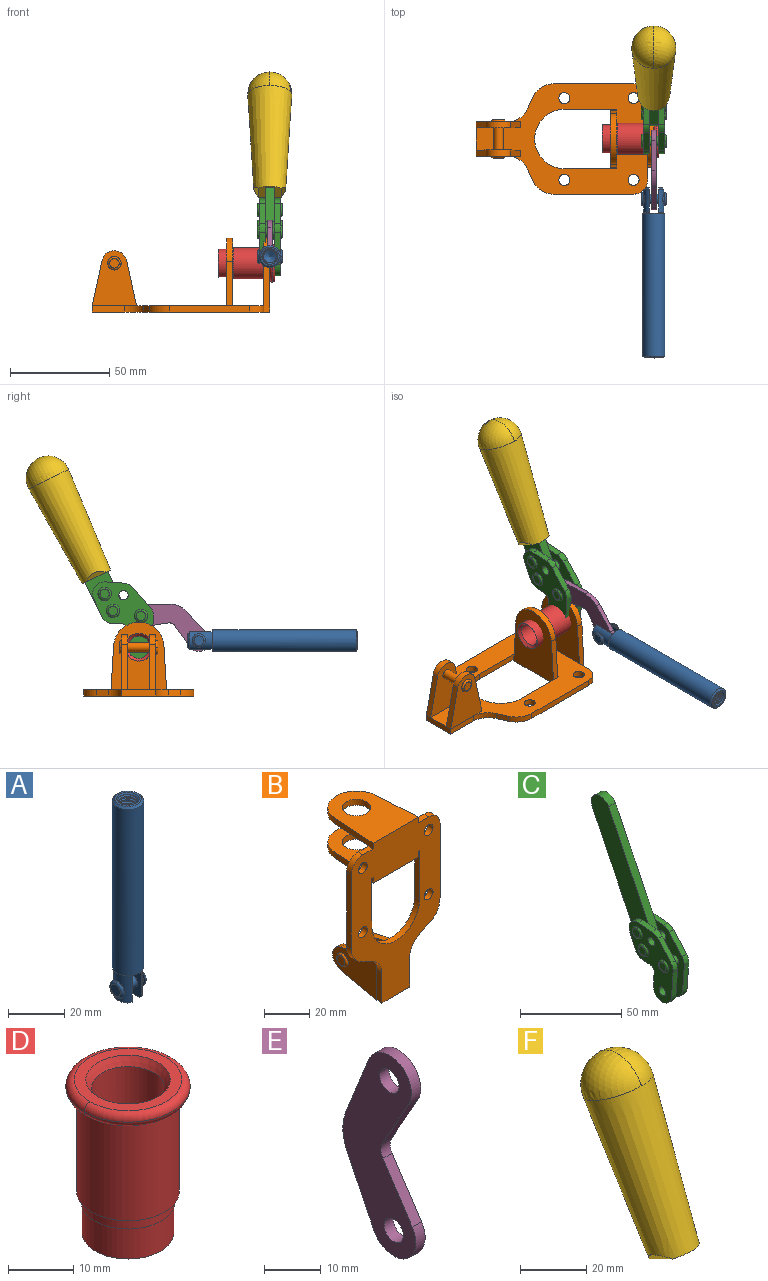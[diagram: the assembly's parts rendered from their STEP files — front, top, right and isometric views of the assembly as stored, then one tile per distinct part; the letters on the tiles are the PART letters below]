
ASSEMBLY  parts=6 mates=6
PART A: 48 faces, bbox 12.6x11.1x86.1 mm
  f0: torus R=2.41mm, axis (-1,0,0), area 15mm2, adj f30,f32,f34
  f1: torus R=2.41mm, axis (-1,0,0), area 15mm2, adj f29,f31,f33
  f2: cylinder r=5.54mm len=72.39mm, axis (0,0,1), area 2518.5mm2, adj f3,f4,f42,f43
  f3: cone r=5.54mm half-angle=45deg, axis (0,0,1), area 7.6mm2, adj f2,f5,f41
  f4: cone r=5.54mm half-angle=45deg, axis (0,0,-1), area 34.9mm2, adj f2,f39
  f5: cylinder r=5.08mm len=11.48mm, axis (0,0,1), area 108.3mm2, adj f3,f7,f8,f41
  f6: cylinder r=2.41mm len=4.83mm, axis (-1,0,0), area 71.2mm2, adj f40,f41
  f7: cylinder r=2.41mm len=4.83mm, axis (-1,0,0), area 7.6mm2, adj f5,f34
  f8: cone r=5.08mm half-angle=45deg, axis (0,0,1), area 10.6mm2, adj f5,f37,f41
  f9: cone r=3.98mm half-angle=45deg, axis (0,0,1), area 17.6mm2, adj f27,f39,f45,f46,f47
  f10: cylinder r=2.41mm len=4.83mm, axis (-1,0,0), area 7.6mm2, adj f33,f38
  f11: cylinder r=3.2mm len=6.4mm, axis (0,0,1), area 78.4mm2, adj f12,f28,f44,f45,f47
  f12: cylinder r=3.2mm len=6.4mm, axis (0,0,1), area 10.5mm2, adj f11,f13,f45,f47
  f13: cylinder r=3.2mm len=6.4mm, axis (0,0,1), area 10.5mm2, adj f12,f14,f45,f47
  f14: cylinder r=3.2mm len=6.4mm, axis (0,0,1), area 10.5mm2, adj f13,f15,f45,f47
  f15: cylinder r=3.2mm len=6.4mm, axis (0,0,1), area 10.5mm2, adj f14,f16,f45,f47
  f16: cylinder r=3.2mm len=6.4mm, axis (0,0,1), area 10.5mm2, adj f15,f17,f45,f47
  f17: cylinder r=3.2mm len=6.4mm, axis (0,0,1), area 10.5mm2, adj f16,f18,f45,f47
  f18: cylinder r=3.2mm len=6.4mm, axis (0,0,1), area 10.5mm2, adj f17,f19,f45,f47
  f19: cylinder r=3.2mm len=6.4mm, axis (0,0,1), area 10.5mm2, adj f18,f20,f45,f47
  f20: cylinder r=3.2mm len=6.4mm, axis (0,0,1), area 10.5mm2, adj f19,f21,f45,f47
  f21: cylinder r=3.2mm len=6.4mm, axis (0,0,1), area 10.5mm2, adj f20,f22,f45,f47
  f22: cylinder r=3.2mm len=6.4mm, axis (0,0,1), area 10.5mm2, adj f21,f23,f45,f47
  f23: cylinder r=3.2mm len=6.4mm, axis (0,0,1), area 10.5mm2, adj f22,f24,f45,f47
  f24: cylinder r=3.2mm len=6.4mm, axis (0,0,1), area 10.5mm2, adj f23,f25,f45,f47
  f25: cylinder r=3.2mm len=6.4mm, axis (0,0,1), area 10.5mm2, adj f24,f26,f45,f47
  f26: cylinder r=3.2mm len=6.4mm, axis (0,0,1), area 10.5mm2, adj f25,f27,f45,f47
  f27: cylinder r=3.2mm len=6.4mm, axis (0,0,1), area 7.4mm2, adj f9,f26,f45,f47
  f28: cone r=3.2mm half-angle=60deg, axis (0,0,1), area 37.2mm2, adj f11
  f29: plane 4.83x4.83mm, normal (-1,0,0), area 18.3mm2, adj f1,f31
  f30: plane 4.83x4.83mm, normal (1,0,0), area 18.3mm2, adj f0,f32
  f31: torus R=2.41mm, axis (-1,0,0), area 15mm2, adj f1,f29,f33
  f32: torus R=2.41mm, axis (-1,0,0), area 15mm2, adj f0,f30,f34
  f33: plane 6.83x6.83mm, normal (1,0,0), area 18.3mm2, adj f1,f10,f31
  f34: plane 6.83x6.83mm, normal (-1,0,0), area 18.3mm2, adj f0,f7,f32
  f35: cone r=5.08mm half-angle=45deg, axis (0,0,1), area 10.6mm2, adj f36,f38,f40
  f36: plane 7.25x1.97mm, normal (0,0,-1), area 10mm2, adj f35,f40
  f37: plane 7.25x1.97mm, normal (0,0,-1), area 10mm2, adj f8,f41
  f38: cylinder r=5.08mm len=11.48mm, axis (0,0,1), area 108.3mm2, adj f10,f35,f40,f42
  f39: plane 9.55x9.55mm, normal (0,0,1), area 22mm2, adj f4,f9
  f40: plane 12.76x10.09mm, normal (1,0,0), area 95.7mm2, adj f6,f35,f36,f38,f42,f43
  f41: plane 12.76x10.09mm, normal (-1,0,0), area 95.7mm2, adj f3,f5,f6,f8,f37,f43
  f42: cone r=5.54mm half-angle=45deg, axis (0,0,1), area 7.6mm2, adj f2,f38,f40
  f43: plane 11.07x4.7mm, normal (0,0,-1), area 50.4mm2, adj f2,f40,f41
  f44: plane 0.89x0.62mm, normal (-1,0,0), area 0.3mm2, adj f11,f45,f46,f47
  f45: bspline ~24.8x7.63mm, area 266.6mm2, adj f9,f11,f12,f13,f14,f15,f16,f17
  f46: bspline ~24.87x7.63mm, area 73.6mm2, adj f9,f44,f45,f47
  f47: bspline ~24.98x7.63mm, area 272.5mm2, adj f9,f11,f12,f13,f14,f15,f16,f17
PART B: 55 faces, bbox 55.7x37.4x89.8 mm
  f0: torus R=2.41mm, axis (-1,0,0), area 15mm2, adj f11,f15,f25
  f1: torus R=2.41mm, axis (-1,0,0), area 15mm2, adj f10,f12,f22
  f2: cylinder r=2.78mm len=5.56mm, axis (0,-1,0), area 54.2mm2, adj f30,f54
  f3: cylinder r=14.99mm len=29.97mm, axis (0,-1,0), area 145.9mm2, adj f30,f49,f53,f54
  f4: cylinder r=2.78mm len=5.56mm, axis (0,-1,0), area 54.2mm2, adj f30,f54
  f5: cylinder r=2.78mm len=5.56mm, axis (0,-1,0), area 54.2mm2, adj f30,f54
  f6: cylinder r=2.78mm len=5.56mm, axis (0,-1,0), area 54.2mm2, adj f30,f54
  f7: cylinder r=6.35mm len=12.7mm, axis (0,0,1), area 123.6mm2, adj f27,f51
  f8: cylinder r=6.35mm len=12.7mm, axis (0,0,-1), area 124.7mm2, adj f21,f35
  f9: cylinder r=2.41mm len=11.18mm, axis (-1,0,0), area 169.4mm2, adj f16,f19
  f10: plane 4.83x4.83mm, normal (1,0,0), area 18.3mm2, adj f1,f12
  f11: plane 4.83x4.83mm, normal (-1,0,0), area 18.3mm2, adj f0,f15
  f12: torus R=2.41mm, axis (-1,0,0), area 15mm2, adj f1,f10,f22
  f13: cylinder r=6.35mm len=12.41mm, axis (1,0,0), area 53.4mm2, adj f18,f19,f22,f23
  f14: cylinder r=6.35mm len=12.41mm, axis (-1,0,0), area 53.4mm2, adj f16,f17,f24,f25
  f15: torus R=2.41mm, axis (-1,0,0), area 15mm2, adj f0,f11,f25
  f16: plane 27.86x22.35mm, normal (1,0,0), area 425.4mm2, adj f9,f14,f17,f24,f30
  f17: plane 22.86x4.97mm, normal (0,0.21,0.98), area 72.5mm2, adj f14,f16,f25,f30
  f18: plane 22.86x4.97mm, normal (0,0.21,0.98), area 72.5mm2, adj f13,f19,f22,f30
  f19: plane 27.86x22.35mm, normal (-1,0,0), area 425.4mm2, adj f9,f13,f18,f23,f30
  f20: cylinder r=12.7mm len=25.35mm, axis (0,0,-1), area 119.8mm2, adj f21,f34,f35,f36
  f21: plane 34.21x28.07mm, normal (0,0,-1), area 702.4mm2, adj f8,f20,f30,f34,f36
  f22: plane 27.96x22.45mm, normal (1,0,0), area 407.2mm2, adj f1,f12,f13,f18,f23,f30,f42,f43
  f23: plane 22.86x4.97mm, normal (0,0.21,-0.98), area 72.5mm2, adj f13,f19,f22,f44
  f24: plane 22.86x4.97mm, normal (0,0.21,-0.98), area 72.5mm2, adj f14,f16,f25,f44
  f25: plane 27.86x22.35mm, normal (-1,0,0), area 407.1mm2, adj f0,f14,f15,f17,f24,f30,f45,f46
  f26: plane 3.1x0.95mm, normal (0,0,-1), area 2.7mm2, adj f30,f49,f50,f54
  f27: plane 34.21x28.07mm, normal (0,0,1), area 702.4mm2, adj f7,f28,f30,f50,f52
  f28: cylinder r=12.7mm len=25.35mm, axis (0,0,1), area 118.8mm2, adj f27,f50,f51,f52
  f29: plane 3.1x0.95mm, normal (0,0,-1), area 2.7mm2, adj f30,f52,f53,f54
  f30: plane 86.54x55.63mm, normal (0,1,0), area 2362.9mm2, adj f2,f3,f4,f5,f6,f16,f17,f18
  f31: plane 40.56x3.1mm, normal (-1,0,0), area 125.7mm2, adj f30,f32,f48,f54
  f32: cylinder r=7.11mm len=7.11mm, axis (0,-1,0), area 34.6mm2, adj f30,f31,f33,f54
  f33: plane 6.67x3.1mm, normal (0,0,1), area 20.4mm2, adj f30,f32,f34,f54
  f34: plane 25.39x3.13mm, normal (-1,0.06,0), area 79.5mm2, adj f20,f21,f33,f35,f54
  f35: plane 37.31x28.45mm, normal (0,0,1), area 789.9mm2, adj f8,f20,f34,f36,f54
  f36: plane 25.39x3.13mm, normal (1,0.06,0), area 79.5mm2, adj f20,f21,f35,f37,f54
  f37: plane 6.67x3.1mm, normal (0,0,1), area 20.4mm2, adj f30,f36,f38,f54
  f38: cylinder r=7.11mm len=7.11mm, axis (0,-1,0), area 34.6mm2, adj f30,f37,f39,f54
  f39: plane 40.56x3.1mm, normal (1,0,0), area 125.7mm2, adj f30,f38,f40,f54
  f40: cylinder r=11.18mm len=10.16mm, axis (0,-1,0), area 39.5mm2, adj f30,f39,f41,f54
  f41: plane 6.09x3.1mm, normal (0.42,0,-0.91), area 20.8mm2, adj f30,f40,f42,f54
  f42: cylinder r=11.18mm len=9.41mm, axis (0,-1,0), area 37.2mm2, adj f22,f30,f41,f43,f54
  f43: plane 16.5x3.1mm, normal (1,0,0), area 51.1mm2, adj f22,f42,f44,f54
  f44: plane 17.37x3.1mm, normal (0,0,-1), area 53.8mm2, adj f23,f24,f30,f43,f45,f54
  f45: plane 16.5x3.1mm, normal (-1,0,0), area 51.1mm2, adj f25,f44,f46,f54
  f46: cylinder r=11.18mm len=9.41mm, axis (0,-1,0), area 37.2mm2, adj f25,f30,f45,f47,f54
  f47: plane 6.09x3.1mm, normal (-0.42,0,-0.91), area 20.8mm2, adj f30,f46,f48,f54
  f48: cylinder r=11.18mm len=10.16mm, axis (0,-1,0), area 39.5mm2, adj f30,f31,f47,f54
  f49: plane 26.54x3.1mm, normal (-1,0,0), area 82.3mm2, adj f3,f26,f30,f54
  f50: plane 25.39x3.1mm, normal (1,0.06,0), area 78.8mm2, adj f26,f27,f28,f51,f54
  f51: plane 37.31x28.45mm, normal (0,0,-1), area 789.9mm2, adj f7,f28,f50,f52,f54
  f52: plane 25.39x3.1mm, normal (-1,0.06,0), area 78.8mm2, adj f27,f28,f29,f51,f54
  f53: plane 26.54x3.1mm, normal (1,0,0), area 82.3mm2, adj f3,f29,f30,f54
  f54: plane 89.66x55.63mm, normal (0,-1,0), area 2678.5mm2, adj f2,f3,f4,f5,f6,f26,f29,f31
PART C: 59 faces, bbox 12.9x60.2x99.6 mm
  f0: torus R=2.39mm, axis (-1,0,0), area 14.9mm2, adj f20,f43,f51
  f1: torus R=2.39mm, axis (-1,0,0), area 14.9mm2, adj f19,f42,f51
  f2: torus R=2.39mm, axis (-1,0,0), area 14.9mm2, adj f18,f35,f51
  f3: torus R=2.39mm, axis (-1,0,0), area 14.9mm2, adj f14,f17,f23
  f4: torus R=2.39mm, axis (-1,0,0), area 14.9mm2, adj f13,f16,f23
  f5: torus R=2.39mm, axis (-1,0,0), area 14.9mm2, adj f12,f15,f23
  f6: cylinder r=2.39mm len=4.78mm, axis (1,0,0), area 46.5mm2, adj f48,f50,f51
  f7: cylinder r=2.39mm len=4.78mm, axis (1,0,0), area 46.5mm2, adj f50,f51
  f8: cylinder r=6.35mm len=12.68mm, axis (1,0,0), area 61.8mm2, adj f38,f39,f50,f51
  f9: cylinder r=2.39mm len=4.78mm, axis (-1,0,0), area 70.5mm2, adj f46,f50
  f10: cylinder r=2.39mm len=4.78mm, axis (-1,0,0), area 46.5mm2, adj f23,f45,f46
  f11: cylinder r=2.39mm len=4.78mm, axis (-1,0,0), area 46.5mm2, adj f23,f46
  f12: plane 4.78x4.78mm, normal (1,0,0), area 17.9mm2, adj f5,f15
  f13: plane 4.78x4.78mm, normal (1,0,0), area 17.9mm2, adj f4,f16
  f14: plane 4.78x4.78mm, normal (1,0,0), area 17.9mm2, adj f3,f17
  f15: torus R=2.39mm, axis (-1,0,0), area 14.9mm2, adj f5,f12,f23
  f16: torus R=2.39mm, axis (-1,0,0), area 14.9mm2, adj f4,f13,f23
  f17: torus R=2.39mm, axis (-1,0,0), area 14.9mm2, adj f3,f14,f23
  f18: plane 4.78x4.78mm, normal (-1,0,0), area 17.9mm2, adj f2,f35
  f19: plane 4.78x4.78mm, normal (-1,0,0), area 17.9mm2, adj f1,f42
  f20: plane 4.78x4.78mm, normal (-1,0,0), area 17.9mm2, adj f0,f43
  f21: plane 2.26x0.2mm, normal (1,0,0), area 0.2mm2, adj f31,f44
  f22: plane 2.26x0.2mm, normal (-1,0,0), area 0.2mm2, adj f41,f44
  f23: plane 39.37x30.77mm, normal (1,0,0), area 565.5mm2, adj f3,f4,f5,f10,f11,f15,f16,f17
  f24: cylinder r=6.1mm len=4.15mm, axis (-1,0,0), area 14.7mm2, adj f23,f25,f32,f46
  f25: plane 10.25x9.01mm, normal (0,-0.75,0.66), area 42.3mm2, adj f23,f24,f26,f46
  f26: cylinder r=6.35mm len=4.64mm, axis (-1,0,0), area 15.6mm2, adj f23,f25,f27,f46
  f27: plane 15.84x3.1mm, normal (0,-1,-0.07), area 49.2mm2, adj f23,f26,f28,f46
  f28: cylinder r=6.35mm len=12.68mm, axis (-1,0,0), area 61.8mm2, adj f23,f27,f29,f46
  f29: plane 8.11x3.1mm, normal (0,1,0.07), area 25.2mm2, adj f23,f28,f30,f46
  f30: cylinder r=3.05mm len=3.25mm, axis (-1,0,0), area 14.8mm2, adj f23,f29,f31,f46
  f31: plane 5.99x3.1mm, normal (0,0.07,-1), area 18.6mm2, adj f21,f23,f30,f44,f46
  f32: plane 9.5x3.1mm, normal (0,-0.07,1), area 29.5mm2, adj f23,f24,f33,f46,f47
  f33: cylinder r=6.1mm len=8.63mm, axis (-1,0,0), area 39.1mm2, adj f23,f32,f34,f47
  f34: plane 8.65x3.96mm, normal (0,0.91,-0.42), area 29.5mm2, adj f23,f33,f44,f47
  f35: torus R=2.39mm, axis (-1,0,0), area 14.9mm2, adj f2,f18,f51
  f36: plane 10.25x9.01mm, normal (0,-0.75,0.66), area 42.3mm2, adj f37,f49,f50,f51
  f37: cylinder r=6.35mm len=4.64mm, axis (1,0,0), area 15.6mm2, adj f36,f38,f50,f51
  f38: plane 15.84x3.1mm, normal (0,-1,-0.07), area 49.2mm2, adj f8,f37,f50,f51
  f39: plane 8.11x3.1mm, normal (0,1,0.07), area 25.2mm2, adj f8,f40,f50,f51
  f40: cylinder r=3.05mm len=3.25mm, axis (1,0,0), area 14.8mm2, adj f39,f41,f50,f51
  f41: plane 5.99x3.1mm, normal (0,0.07,-1), area 18.6mm2, adj f22,f40,f44,f50,f51
  f42: torus R=2.39mm, axis (-1,0,0), area 14.9mm2, adj f1,f19,f51
  f43: torus R=2.39mm, axis (-1,0,0), area 14.9mm2, adj f0,f20,f51
  f44: cylinder r=6.35mm len=12.12mm, axis (-1,0,0), area 128.9mm2, adj f21,f22,f23,f31,f34,f41,f46,f47
  f45: plane 2.65x1.35mm, normal (1,0,0), area 1mm2, adj f10,f55
  f46: plane 39.08x20.42mm, normal (-1,0,0), area 412.5mm2, adj f9,f10,f11,f24,f25,f26,f27,f28
  f47: plane 77.62x39.82mm, normal (1,0,0), area 850mm2, adj f32,f33,f34,f44,f53,f54,f55
  f48: plane 2.65x1.35mm, normal (-1,0,0), area 1mm2, adj f6,f55
  f49: cylinder r=6.1mm len=4.15mm, axis (1,0,0), area 14.7mm2, adj f36,f50,f51,f56
  f50: plane 39.08x20.42mm, normal (1,0,0), area 412.5mm2, adj f6,f7,f8,f9,f36,f37,f38,f39
  f51: plane 39.37x30.77mm, normal (-1,0,0), area 565.5mm2, adj f0,f1,f2,f6,f7,f8,f35,f36
  f52: plane 8.65x3.96mm, normal (0,0.91,-0.42), area 29.5mm2, adj f44,f51,f57,f58
  f53: plane 68.49x33.4mm, normal (0,0.9,-0.44), area 358.1mm2, adj f44,f47,f54,f58
  f54: cylinder r=6.35mm len=12.06mm, axis (1,0,0), area 93.7mm2, adj f47,f53,f55,f58
  f55: plane 68.49x33.4mm, normal (0,-0.9,0.44), area 358.1mm2, adj f44,f45,f46,f47,f48,f50,f54,f58
  f56: plane 9.5x3.1mm, normal (0,-0.07,1), area 29.5mm2, adj f49,f50,f51,f57,f58
  f57: cylinder r=6.1mm len=8.63mm, axis (1,0,0), area 39.1mm2, adj f51,f52,f56,f58
  f58: plane 77.62x39.82mm, normal (-1,0,0), area 850mm2, adj f44,f52,f53,f54,f55,f56,f57
PART D: 15 faces, bbox 20.6x20.6x28.7 mm
  f0: torus R=8.26mm, axis (0,0,1), area 56.8mm2, adj f1,f10,f12
  f1: torus R=8.26mm, axis (0,0,1), area 56.8mm2, adj f0,f6,f13
  f2: cylinder r=5.59mm len=25.91mm, axis (0,0,1), area 909.6mm2, adj f3,f4
  f3: cone r=6.86mm half-angle=45deg, axis (0,0,-1), area 70.2mm2, adj f2,f14
  f4: cone r=6.47mm half-angle=30deg, axis (0,0,1), area 66.7mm2, adj f2,f13
  f5: cylinder r=7.04mm len=14.07mm, axis (0,0,1), area 252.6mm2, adj f11,f14
  f6: torus R=8.26mm, axis (0,0,1), area 56.8mm2, adj f1,f12,f13
  f7: cylinder r=7.16mm len=14.33mm, axis (0,0,1), area 91.5mm2, adj f9,f11
  f8: cylinder r=7.86mm len=18.42mm, axis (0,0,1), area 909.6mm2, adj f9,f10
  f9: plane 15.72x15.72mm, normal (0,0,-1), area 33mm2, adj f7,f8
  f10: plane 16.51x16.51mm, normal (0,0,-1), area 19.9mm2, adj f0,f8,f12
  f11: plane 14.33x14.33mm, normal (0,0,-1), area 5.7mm2, adj f5,f7
  f12: torus R=8.26mm, axis (0,0,1), area 56.8mm2, adj f0,f6,f10
  f13: plane 16.51x16.51mm, normal (0,0,1), area 82.7mm2, adj f1,f4,f6
  f14: plane 14.07x14.07mm, normal (0,0,-1), area 7.8mm2, adj f3,f5
PART E: 12 faces, bbox 2.3x18.2x42.8 mm
  f0: cylinder r=2.4mm len=4.8mm, axis (1,0,0), area 34.9mm2, adj f4,f11
  f1: cylinder r=10.41mm len=8.47mm, axis (1,0,0), area 20.2mm2, adj f4,f9,f10,f11
  f2: cylinder r=3.05mm len=3.16mm, axis (1,0,0), area 7.7mm2, adj f4,f6,f7,f11
  f3: cylinder r=2.4mm len=4.8mm, axis (1,0,0), area 34.9mm2, adj f4,f11
  f4: plane 42.81x18.23mm, normal (-1,0,0), area 414.1mm2, adj f0,f1,f2,f3,f5,f6,f7,f8
  f5: cylinder r=5.54mm len=10.67mm, axis (1,0,0), area 41.8mm2, adj f4,f6,f10,f11
  f6: plane 11.66x6.53mm, normal (0,-0.87,-0.49), area 30.9mm2, adj f2,f4,f5,f11
  f7: plane 11.17x7.33mm, normal (0,-0.84,0.55), area 30.9mm2, adj f2,f4,f8,f11
  f8: cylinder r=5.54mm len=10.51mm, axis (1,0,0), area 41.8mm2, adj f4,f7,f9,f11
  f9: plane 13.67x6.67mm, normal (0,0.9,-0.44), area 35.1mm2, adj f1,f4,f8,f11
  f10: plane 14.1x5.7mm, normal (0,0.93,0.37), area 35.1mm2, adj f1,f4,f5,f11
  f11: plane 42.81x18.23mm, normal (1,0,0), area 414.1mm2, adj f0,f1,f2,f3,f5,f6,f7,f8
PART F: 11 faces, bbox 22.3x42.6x64.5 mm
  f0: sphere r=11.13mm, area 411.4mm2, adj f1,f8
  f1: cone r=11.11mm half-angle=3.3deg, axis (0,0.44,0.9), area 3251.8mm2, adj f0,f7,f8,f9,f10
  f2: cylinder r=6.16mm len=11.7mm, axis (1,0,0), area 89.5mm2, adj f3,f4,f5,f6
  f3: plane 60.23x36.75mm, normal (-1,0,0), area 763.6mm2, adj f2,f4,f6,f10
  f4: plane 51.37x25.05mm, normal (0,0.9,-0.44), area 264.2mm2, adj f2,f3,f5,f10
  f5: plane 60.23x36.75mm, normal (1,0,0), area 763.6mm2, adj f2,f4,f6,f10
  f6: plane 51.37x25.05mm, normal (0,-0.9,0.44), area 264.2mm2, adj f2,f3,f5,f10
  f7: plane 9.95x5.95mm, normal (0.71,-0.31,-0.64), area 25.8mm2, adj f1,f10
  f8: sphere r=11.13mm, area 411.4mm2, adj f0,f1
  f9: plane 9.95x5.95mm, normal (-0.71,-0.31,-0.64), area 25.8mm2, adj f1,f10
  f10: plane 14.27x11.38mm, normal (0,-0.44,-0.9), area 106.7mm2, adj f1,f3,f4,f5,f6,f7,f9
PLACE A rot(axis=(1,0,0),90deg) t=(14.29,-14.77,3.49)mm
PLACE B rot(axis=(0.58,0.58,0.58),120deg) t=(-32.11,0.08,0.09)mm fixed
PLACE C rot(axis=(1,0,0),0deg) t=(14.29,-24.53,56.8)mm
PLACE D rot(axis=(0.71,0,0.71),180deg) t=(-32.11,24.69,24.71)mm
PLACE E rot(axis=(0,-0.57,-0.82),180deg) t=(14.29,-6.62,12.01)mm
PLACE F rot(axis=(-1,0,0),0deg) t=(14.25,-24.53,56.8)mm
MATE fastened D.f2 <-> B.f7  axis (-1,0,0) through (14.29,0.08,24.71)mm
MATE slider B.f7 <-> C.f7  axis (1,0,0) through (14.29,0.08,24.71)mm
MATE revolute B.f0 <-> C.f7  axis (0,-1,0) through (-64.2,0.08,24.71)mm
MATE revolute E.f5 <-> C.f4  axis (-1,0,0) through (14.29,-1.03,40.54)mm
MATE fastened F.f2 <-> C.f54  axis (1,0,0) through (11.94,46.51,111.57)mm
MATE revolute E.f3 <-> A.f6  axis (-1,0,0) through (14.29,-30.24,28.1)mm
